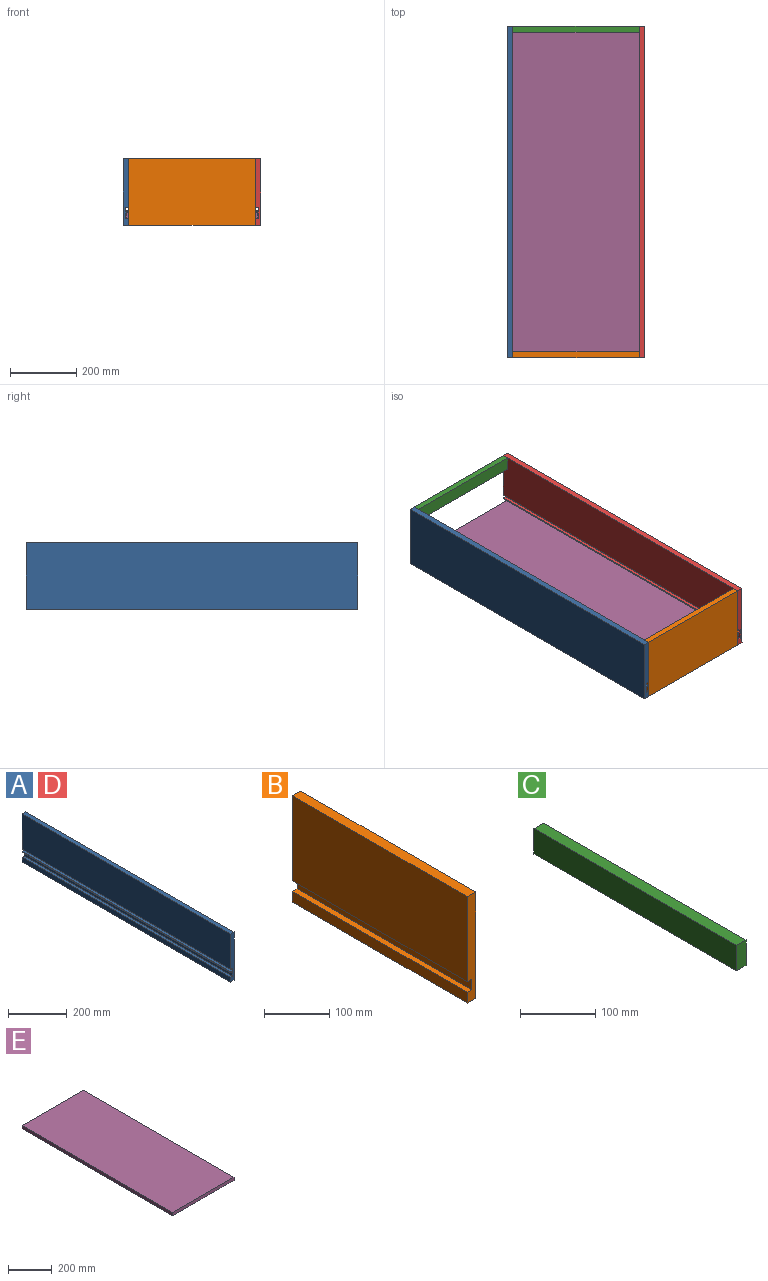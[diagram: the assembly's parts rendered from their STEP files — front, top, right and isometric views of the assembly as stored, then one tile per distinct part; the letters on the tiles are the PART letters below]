
ASSEMBLY  parts=5 mates=5
PART A: 14 faces, bbox 18x1000x200 mm
  f0: plane 1000x10mm, normal (0,0,1), area 10000mm2, adj f1,f11,f12,f13
  f1: plane 1000x3.68mm, normal (-1,0,0), area 3676.9mm2, adj f0,f2,f12,f13
  f2: plane 1000x10mm, normal (0,0,-1), area 10000mm2, adj f1,f3,f12,f13
  f3: plane 1000x20mm, normal (-1,0,0), area 20000mm2, adj f2,f4,f12,f13
  f4: plane 1000x10mm, normal (0,0,1), area 10000mm2, adj f3,f5,f12,f13
  f5: plane 1000x20mm, normal (-1,0,0), area 20000mm2, adj f4,f6,f12,f13
  f6: plane 1000x18mm, normal (0,0,-1), area 18000mm2, adj f5,f7,f12,f13
  f7: plane 1000x200mm, normal (1,0,0), area 200000mm2, adj f6,f8,f12,f13
  f8: plane 1000x18mm, normal (0,0,1), area 18000mm2, adj f7,f9,f12,f13
  f9: plane 1000x146.32mm, normal (-1,0,0), area 146323.1mm2, adj f8,f10,f12,f13
  f10: plane 1000x10mm, normal (0,0,-1), area 10000mm2, adj f9,f11,f12,f13
  f11: plane 1000x10mm, normal (-1,0,0), area 10000mm2, adj f0,f10,f12,f13
  f12: plane 200x18mm, normal (0,1,0), area 3300mm2, adj f0,f1,f2,f3,f4,f5,f6,f7
  f13: plane 200x18mm, normal (0,-1,0), area 3300mm2, adj f0,f1,f2,f3,f4,f5,f6,f7
PART B: 10 faces, bbox 18x380x200 mm
  f0: plane 380x10mm, normal (0,0,1), area 3800mm2, adj f1,f7,f8,f9
  f1: plane 380x20mm, normal (-1,0,0), area 7600mm2, adj f0,f2,f8,f9
  f2: plane 380x18mm, normal (0,0,-1), area 6840mm2, adj f1,f3,f8,f9
  f3: plane 380x200mm, normal (1,0,0), area 76000mm2, adj f2,f4,f8,f9
  f4: plane 380x18mm, normal (0,0,1), area 6840mm2, adj f3,f5,f8,f9
  f5: plane 380x160mm, normal (-1,0,0), area 60800mm2, adj f4,f6,f8,f9
  f6: plane 380x10mm, normal (0,0,-1), area 3800mm2, adj f5,f7,f8,f9
  f7: plane 380x20mm, normal (-1,0,0), area 7600mm2, adj f0,f6,f8,f9
  f8: plane 200x18mm, normal (0,-1,0), area 3400mm2, adj f0,f1,f2,f3,f4,f5,f6,f7
  f9: plane 200x18mm, normal (0,1,0), area 3400mm2, adj f0,f1,f2,f3,f4,f5,f6,f7
PART C: 6 faces, bbox 18x380x41.3 mm
  f0: plane 380x18mm, normal (0,0,-1), area 6840mm2, adj f1,f3,f4,f5
  f1: plane 380x41.32mm, normal (1,0,0), area 15702.8mm2, adj f0,f2,f4,f5
  f2: plane 380x18mm, normal (0,0,1), area 6840mm2, adj f1,f3,f4,f5
  f3: plane 380x41.32mm, normal (-1,0,0), area 15702.8mm2, adj f0,f2,f4,f5
  f4: plane 41.32x18mm, normal (0,1,0), area 743.8mm2, adj f0,f1,f2,f3
  f5: plane 41.32x18mm, normal (0,-1,0), area 743.8mm2, adj f0,f1,f2,f3
PART D: same geometry as A
PART E: 6 faces, bbox 398x980x18 mm
  f0: plane 980x398mm, normal (0,0,1), area 390040mm2, adj f1,f3,f4,f5
  f1: plane 980x18mm, normal (-1,0,0), area 17640mm2, adj f0,f2,f4,f5
  f2: plane 980x398mm, normal (0,0,-1), area 390040mm2, adj f1,f3,f4,f5
  f3: plane 980x18mm, normal (1,0,0), area 17640mm2, adj f0,f2,f4,f5
  f4: plane 398x18mm, normal (0,1,0), area 7164mm2, adj f0,f1,f2,f3
  f5: plane 398x18mm, normal (0,-1,0), area 7164mm2, adj f0,f1,f2,f3
PLACE A rot(axis=(0,0,1),180deg) t=(290.26,-85.36,0)mm
PLACE B rot(axis=(0,0,-1),90deg) t=(688.26,-1085.36,0)mm
PLACE C rot(axis=(0,0,1),90deg) t=(688.26,-85.36,0)mm
PLACE D rot(axis=(0,-0.57,-0.82),0deg) t=(706.26,-1085.36,0)mm
PLACE E rot(axis=(0,-0.57,-0.82),0deg) t=(523.82,-1077.36,-170.86)mm
MATE fastened B.f2 <-> A.f6  axis (0,0,-1) through (308.26,-1085.36,-200)mm
MATE fastened C.f2 <-> D.f8  axis (0,0,1) through (688.26,-85.36,0)mm
MATE fastened E.f5 <-> B.f7  axis (0,-1,0) through (498.26,-1077.36,-170)mm
MATE fastened C.f2 <-> D.f8  axis (0,0,1) through (688.26,-85.36,0)mm
MATE fastened A.f8 <-> C.f2  axis (0,0,1) through (308.26,-85.36,0)mm
